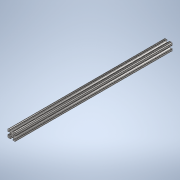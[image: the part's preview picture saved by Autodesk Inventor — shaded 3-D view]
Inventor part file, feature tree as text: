
AUTODESK INVENTOR PART (.ipt)
format: ipt  version: 2020 (Build 240168000, 168)  size: 241,152 bytes
history: native  units: in
note: dims shown in document units (in); Inventor stores cm internally (conversion verified against a paired STEP export)
features: extrude x1, sketch x1
ambient origin geometry x8: Origin, YZ Plane, XZ Plane, XY Plane, X Axis, Y Axis, Z Axis, Center Point
bodies: Solid1 (feature_tree)
feature tree (2):
  extrude  "Extrusion1"  [1 undecoded]
  sketch  "Sketch1"  dims[d0=20.0in d1=0.0in]
note: 1 required parameter value undecoded (feature->parameter linkage not recoverable at this tier; creation-order binding heuristic only, values carry confidence <= 0.55)
